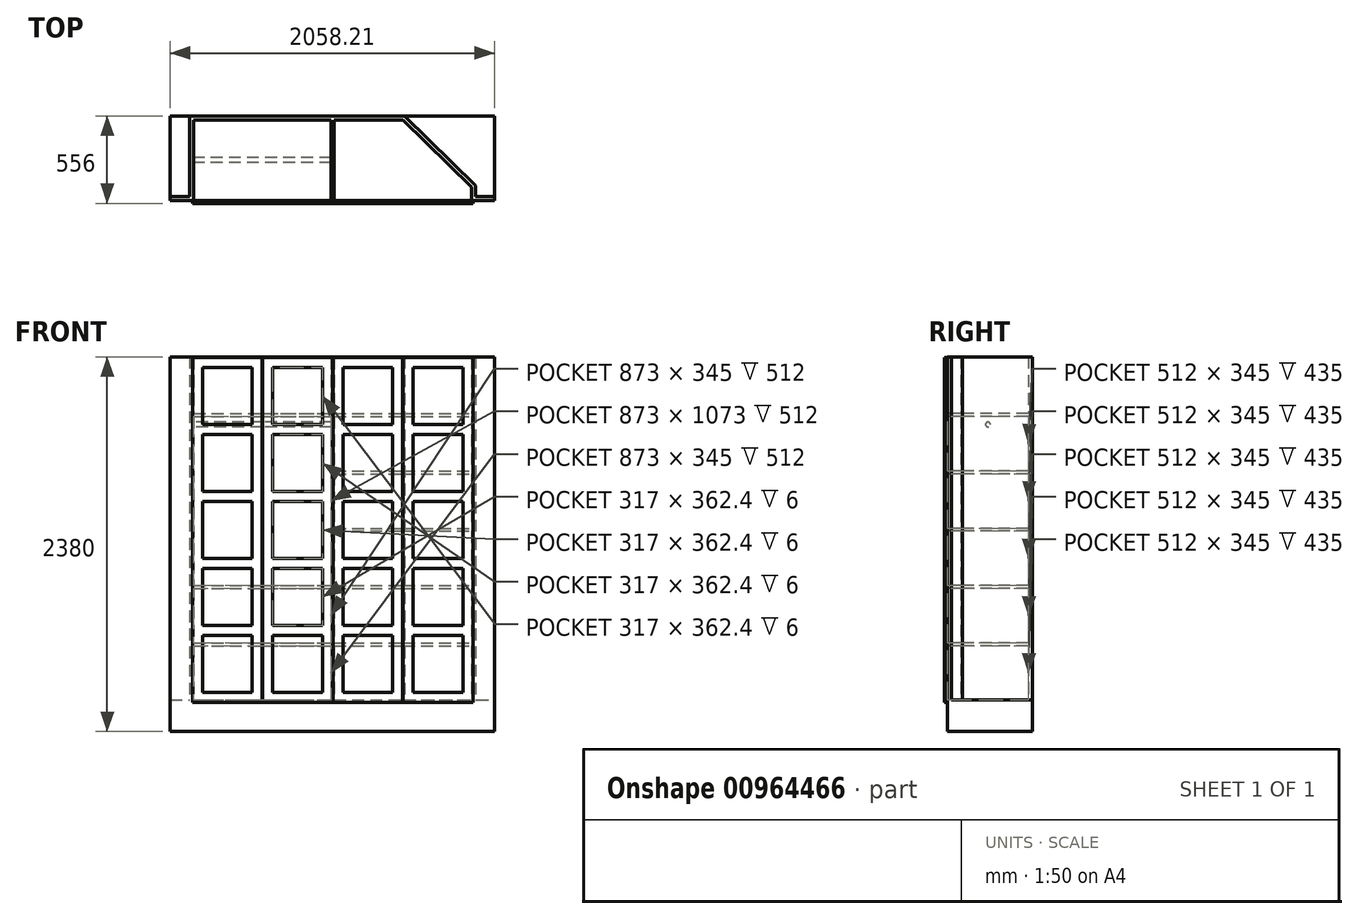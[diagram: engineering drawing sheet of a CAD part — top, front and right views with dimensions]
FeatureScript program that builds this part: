
annotation { "Feature Type Name" : "Feature", "Feature Type Description" : "" }
export const myFeature = defineFeature(function(context is Context, id is Id, definition is map)
    precondition{}
    {
        {
            var Q0;
            Q0=qCreatedBy(makeId("Top.planeOp"),FACE);
            var sketch = newSketch(context, id + "F0", { "sketchPlane" : qUnion([Q0])});
            skLineSegment(sketch, "E0", {"start": v(-882.5, 0) * mm, "end": v(882.5, 0) * mm, "construction": true});
            skLineSegment(sketch, "E1", {"start": v(-882.5, 0) * mm, "end": v(-1031.49, 0) * mm});
            skLineSegment(sketch, "E2", {"start": v(-882.5, 0) * mm, "end": v(-882.5, 512) * mm});
            skLineSegment(sketch, "E3", {"start": v(-882.5, 512) * mm, "end": v(445.5, 512) * mm});
            skLineSegment(sketch, "E4", {"start": v(445.5, 512) * mm, "end": v(882.5, 85) * mm});
            skLineSegment(sketch, "E5", {"start": v(882.5, 0) * mm, "end": v(882.5, 85) * mm});
            skLineSegment(sketch, "E6", {"start": v(882.5, 0) * mm, "end": v(1026.72, 0) * mm});
            skLineSegment(sketch, "E7.0", {"start": v(-907.5, 25) * mm, "end": v(-1031.49, 25) * mm});
            skLineSegment(sketch, "E7.1", {"start": v(-907.5, 25) * mm, "end": v(-907.5, 537) * mm});
            skLineSegment(sketch, "E7.2", {"start": v(907.5, 25) * mm, "end": v(1026.72, 25) * mm});
            skLineSegment(sketch, "E7.3", {"start": v(907.5, 25) * mm, "end": v(907.5, 95.53) * mm});
            skLineSegment(sketch, "E7.4", {"start": v(455.69, 537) * mm, "end": v(907.5, 95.53) * mm});
            skLineSegment(sketch, "E7.5", {"start": v(-907.5, 537) * mm, "end": v(455.69, 537) * mm});
            skLineSegment(sketch, "E8", {"start": v(-1031.49, 0) * mm, "end": v(-1031.49, 25) * mm});
            skLineSegment(sketch, "E9", {"start": v(1026.72, 0) * mm, "end": v(1026.72, 25) * mm});
            skSolve(sketch);
        }
        {
            var Q0;
            Q0 = qSketchRegion(id + "F0", true);
            extrude(context, id + "F1", {"entities" : qUnion([Q0]), "depth" : 2180 * mm, "offsetDistance" : 25 * mm});
        }
        {
            var Q0;
            Q0=makeQuery(id+"F1.opExtrude","CAP_FACE",FACE,{"disambiguationData":[OSD([sQuery(id+"F0.wireOp",EDGE,"E1"),sQuery(id+"F0.wireOp",EDGE,"E2"),sQuery(id+"F0.wireOp",EDGE,"E3"),sQuery(id+"F0.wireOp",EDGE,"E4"),sQuery(id+"F0.wireOp",EDGE,"E5"),sQuery(id+"F0.wireOp",EDGE,"E6"),sQuery(id+"F0.wireOp",EDGE,"E7.0"),sQuery(id+"F0.wireOp",EDGE,"E7.1"),sQuery(id+"F0.wireOp",EDGE,"E7.2"),sQuery(id+"F0.wireOp",EDGE,"E7.3"),sQuery(id+"F0.wireOp",EDGE,"E7.4"),sQuery(id+"F0.wireOp",EDGE,"E7.5"),sQuery(id+"F0.wireOp",EDGE,"E8"),sQuery(id+"F0.wireOp",EDGE,"E9")])],"isStart":true});
            var sketch = newSketch(context, id + "F2", { "sketchPlane" : qUnion([Q0])});
            skLineSegment(sketch, "E10.bottom", {"start": v(-1031.49, 0) * mm, "end": v(1026.72, 0) * mm});
            skLineSegment(sketch, "E10.top", {"start": v(-1031.49, -537) * mm, "end": v(1026.72, -537) * mm});
            skLineSegment(sketch, "E10.left", {"start": v(-1031.49, 0) * mm, "end": v(-1031.49, -537) * mm});
            skLineSegment(sketch, "E10.right", {"start": v(1026.72, 0) * mm, "end": v(1026.72, -537) * mm});
            skSolve(sketch);
        }
        {
            var Q0;
            Q0 = qSketchRegion(id + "F2", true);
            extrude(context, id + "F3", {"entities" : qUnion([Q0]), "operationType" : NewBodyOperationType.ADD, "depth" : 200 * mm, "offsetDistance" : 25 * mm});
        }
        {
            var Q0;
            {var subQ0=sQuery(id+"F2.wireOp",EDGE,"E10.bottom");Q0=makeQuery(id+"F3.boolean.opBoolean","SPLIT",FACE,{"disambiguationData":[TD([makeQuery(id+"F1.opExtrude","SWEPT_FACE",FACE,{"disambiguationData":[OSD([sQuery(id+"F0.wireOp",EDGE,"E1")])]})])],"derivedFrom":makeQuery(id+"F3.opExtrude","CAP_FACE",FACE,{"disambiguationData":[OSD([subQ0,sQuery(id+"F2.wireOp",EDGE,"E10.top"),sQuery(id+"F2.wireOp",EDGE,"E10.left"),sQuery(id+"F2.wireOp",EDGE,"E10.right")])],"isStart":true})});}
            var sketch = newSketch(context, id + "F4", { "sketchPlane" : qUnion([Q0])});
            skLineSegment(sketch, "E11.bottom", {"start": v(-9.5, 0) * mm, "end": v(9.5, 0) * mm});
            skLineSegment(sketch, "E11.top", {"start": v(-9.5, 512) * mm, "end": v(9.5, 512) * mm});
            skLineSegment(sketch, "E11.left", {"start": v(-9.5, 0) * mm, "end": v(-9.5, 512) * mm});
            skLineSegment(sketch, "E11.right", {"start": v(9.5, 0) * mm, "end": v(9.5, 512) * mm});
            skSolve(sketch);
        }
        {
            var Q0;
            Q0 = qSketchRegion(id + "F4", true);
            var Q1;
            Q1=makeQuery(id+"F1.opExtrude","CAP_FACE",FACE,{"disambiguationData":[OSD([sQuery(id+"F0.wireOp",EDGE,"E1"),sQuery(id+"F0.wireOp",EDGE,"E2"),sQuery(id+"F0.wireOp",EDGE,"E3"),sQuery(id+"F0.wireOp",EDGE,"E4"),sQuery(id+"F0.wireOp",EDGE,"E5"),sQuery(id+"F0.wireOp",EDGE,"E6"),sQuery(id+"F0.wireOp",EDGE,"E7.0"),sQuery(id+"F0.wireOp",EDGE,"E7.1"),sQuery(id+"F0.wireOp",EDGE,"E7.2"),sQuery(id+"F0.wireOp",EDGE,"E7.3"),sQuery(id+"F0.wireOp",EDGE,"E7.4"),sQuery(id+"F0.wireOp",EDGE,"E7.5"),sQuery(id+"F0.wireOp",EDGE,"E8"),sQuery(id+"F0.wireOp",EDGE,"E9")])],"isStart":false});
            extrude(context, id + "F5", {"entities" : qUnion([Q0]), "operationType" : NewBodyOperationType.ADD, "endBound" : BoundingType.UP_TO_SURFACE, "depth" : 25 * mm, "endBoundEntityFace" : qUnion([Q1]), "offsetDistance" : 25 * mm});
        }
        {
            var Q0;
            Q0=makeQuery(id+"F5.boolean.opBoolean","MERGE",FACE,{"derivedFrom":[makeQuery(id+"F3.boolean.opBoolean","MERGE",FACE,{"derivedFrom":[makeQuery(id+"F1.opExtrude","SWEPT_FACE",FACE,{"disambiguationData":[OSD([sQuery(id+"F0.wireOp",EDGE,"E1")])]}),makeQuery(id+"F1.opExtrude","SWEPT_FACE",FACE,{"disambiguationData":[OSD([sQuery(id+"F0.wireOp",EDGE,"E6")])]}),makeQuery(id+"F3.opExtrude","SWEPT_FACE",FACE,{"disambiguationData":[OSD([sQuery(id+"F2.wireOp",EDGE,"E10.bottom")])]})]}),makeQuery(id+"F5.opExtrude","SWEPT_FACE",FACE,{"disambiguationData":[OSD([sQuery(id+"F4.wireOp",EDGE,"E11.bottom")])]}),makeQuery(id+"F5.opExtrude","SWEPT_FACE",FACE,{"disambiguationData":[OSD([sQuery(id+"F4.wireOp",EDGE,"kJ6FKThs-MoNL-kqar-oXPB-ncLJq9slYm2o.bottom")])]}),makeQuery(id+"F5.opExtrude","SWEPT_FACE",FACE,{"disambiguationData":[OSD([sQuery(id+"F4.wireOp",EDGE,"Q5dsoZYq-HTbt-CrDa-Fhxc-pEQLqIX1TYuc.bottom")])]})]});
            var sketch = newSketch(context, id + "F6", { "sketchPlane" : qUnion([Q0])});
            skLineSegment(sketch, "E12.bottom", {"start": v(-444.5, -15) * mm, "end": v(-1.5, -15) * mm});
            skLineSegment(sketch, "E12.top", {"start": v(-444.5, 2175) * mm, "end": v(-1.5, 2175) * mm});
            skLineSegment(sketch, "E12.left", {"start": v(-444.5, -15) * mm, "end": v(-444.5, 2175) * mm});
            skLineSegment(sketch, "E12.right", {"start": v(-1.5, -15) * mm, "end": v(-1.5, 2175) * mm});
            skLineSegment(sketch, "E13.bottom", {"start": v(-1.5, -15) * mm, "end": v(-444.5, -15) * mm});
            skLineSegment(sketch, "E13.top", {"start": v(-1.5, 2175) * mm, "end": v(-444.5, 2175) * mm});
            skLineSegment(sketch, "E13.right", {"start": v(-890.5, -15) * mm, "end": v(-890.5, 2175) * mm});
            skLineSegment(sketch, "E14.left", {"start": v(1.5, -15) * mm, "end": v(1.5, 2175) * mm});
            skLineSegment(sketch, "E14.right", {"start": v(-1.5, -15) * mm, "end": v(-1.5, 2195) * mm});
            skLineSegment(sketch, "E15.bottom", {"start": v(447.5, -15) * mm, "end": v(890.5, -15) * mm});
            skLineSegment(sketch, "E15.top", {"start": v(447.5, 2175) * mm, "end": v(890.5, 2175) * mm});
            skLineSegment(sketch, "E15.left", {"start": v(447.5, -15) * mm, "end": v(447.5, 2175) * mm});
            skLineSegment(sketch, "E15.right", {"start": v(890.5, -15) * mm, "end": v(890.5, 2175) * mm});
            skLineSegment(sketch, "E16", {"start": v(-447.5, -15) * mm, "end": v(-447.5, 2175) * mm});
            skLineSegment(sketch, "E17.trimOffspring", {"start": v(-447.5, 2175) * mm, "end": v(-890.5, 2175) * mm});
            skLineSegment(sketch, "E18.trimOffspring", {"start": v(-447.5, -15) * mm, "end": v(-890.5, -15) * mm});
            skLineSegment(sketch, "E19", {"start": v(1.5, -15) * mm, "end": v(444.5, -15) * mm});
            skLineSegment(sketch, "E20", {"start": v(444.5, -15) * mm, "end": v(444.5, 2175) * mm});
            skLineSegment(sketch, "E21", {"start": v(1.5, 2175) * mm, "end": v(444.5, 2175) * mm});
            skSolve(sketch);
        }
        {
            var Q0;
            Q0 = qSketchRegion(id + "F6", true);
            extrude(context, id + "F7", {"entities" : qUnion([Q0]), "operationType" : NewBodyOperationType.ADD, "depth" : 19 * mm, "offsetDistance" : 25 * mm});
        }
        {
            var Q0;
            Q0=makeQuery(id+"F7.opExtrude","CAP_FACE",FACE,{"disambiguationData":[OSD([sQuery(id+"F6.wireOp",EDGE,"E13.bottom"),sQuery(id+"F6.wireOp",EDGE,"E13.top"),sQuery(id+"F6.wireOp",EDGE,"E12.right"),sQuery(id+"F6.wireOp",EDGE,"E13.right")])],"isStart":false});
            var sketch = newSketch(context, id + "F8", { "sketchPlane" : qUnion([Q0])});
            skLineSegment(sketch, "E22.bottom", {"start": v(-827.5, 2112) * mm, "end": v(-510.5, 2112) * mm});
            skLineSegment(sketch, "E22.top", {"start": v(-827.5, 1749.6) * mm, "end": v(-510.5, 1749.6) * mm});
            skLineSegment(sketch, "E22.left", {"start": v(-827.5, 2112) * mm, "end": v(-827.5, 1749.6) * mm});
            skLineSegment(sketch, "E22.right", {"start": v(-510.5, 2112) * mm, "end": v(-510.5, 1749.6) * mm});
            skLineSegment(sketch, "E23.bottom", {"start": v(-827.5, 1686.6) * mm, "end": v(-510.5, 1686.6) * mm});
            skLineSegment(sketch, "E23.top", {"start": v(-827.5, 1324.2) * mm, "end": v(-510.5, 1324.2) * mm});
            skLineSegment(sketch, "E23.left", {"start": v(-827.5, 1686.6) * mm, "end": v(-827.5, 1324.2) * mm});
            skLineSegment(sketch, "E23.right", {"start": v(-510.5, 1686.6) * mm, "end": v(-510.5, 1324.2) * mm});
            skLineSegment(sketch, "E24.bottom", {"start": v(-827.5, 1261.2) * mm, "end": v(-510.5, 1261.2) * mm});
            skLineSegment(sketch, "E24.top", {"start": v(-827.5, 898.8) * mm, "end": v(-510.5, 898.8) * mm});
            skLineSegment(sketch, "E24.left", {"start": v(-827.5, 1261.2) * mm, "end": v(-827.5, 898.8) * mm});
            skLineSegment(sketch, "E24.right", {"start": v(-510.5, 1261.2) * mm, "end": v(-510.5, 898.8) * mm});
            skLineSegment(sketch, "E25.bottom", {"start": v(-827.5, 835.8) * mm, "end": v(-510.5, 835.8) * mm});
            skLineSegment(sketch, "E25.top", {"start": v(-827.5, 473.4) * mm, "end": v(-510.5, 473.4) * mm});
            skLineSegment(sketch, "E25.left", {"start": v(-827.5, 835.8) * mm, "end": v(-827.5, 473.4) * mm});
            skLineSegment(sketch, "E25.right", {"start": v(-510.5, 835.8) * mm, "end": v(-510.5, 473.4) * mm});
            skLineSegment(sketch, "E26.bottom", {"start": v(-827.5, 410.4) * mm, "end": v(-510.5, 410.4) * mm});
            skLineSegment(sketch, "E26.top", {"start": v(-827.5, 48) * mm, "end": v(-510.5, 48) * mm});
            skLineSegment(sketch, "E26.left", {"start": v(-827.5, 410.4) * mm, "end": v(-827.5, 48) * mm});
            skLineSegment(sketch, "E26.right", {"start": v(-510.5, 410.4) * mm, "end": v(-510.5, 48) * mm});
            skLineSegment(sketch, "E27.bottom", {"start": v(-381.5, 2112) * mm, "end": v(-64.5, 2112) * mm});
            skLineSegment(sketch, "E27.top", {"start": v(-381.5, 1749.6) * mm, "end": v(-64.5, 1749.6) * mm});
            skLineSegment(sketch, "E27.left", {"start": v(-381.5, 2112) * mm, "end": v(-381.5, 1749.6) * mm});
            skLineSegment(sketch, "E28.left", {"start": v(64.5, 2112) * mm, "end": v(64.5, 1749.6) * mm});
            skLineSegment(sketch, "E28.right", {"start": v(-64.5, 2112) * mm, "end": v(-64.5, 1749.6) * mm});
            skLineSegment(sketch, "E29.bottom", {"start": v(510.5, 2112) * mm, "end": v(827.5, 2112) * mm});
            skLineSegment(sketch, "E29.top", {"start": v(510.5, 1749.6) * mm, "end": v(827.5, 1749.6) * mm});
            skLineSegment(sketch, "E29.left", {"start": v(510.5, 2112) * mm, "end": v(510.5, 1749.6) * mm});
            skLineSegment(sketch, "E29.right", {"start": v(827.5, 2112) * mm, "end": v(827.5, 1749.6) * mm});
            skLineSegment(sketch, "E30.bottom", {"start": v(-381.5, 1686.6) * mm, "end": v(-64.5, 1686.6) * mm});
            skLineSegment(sketch, "E30.top", {"start": v(-381.5, 1324.2) * mm, "end": v(-64.5, 1324.2) * mm});
            skLineSegment(sketch, "E30.left", {"start": v(-381.5, 1686.6) * mm, "end": v(-381.5, 1324.2) * mm});
            skLineSegment(sketch, "E31.left", {"start": v(64.5, 1686.6) * mm, "end": v(64.5, 1324.2) * mm});
            skLineSegment(sketch, "E31.right", {"start": v(-64.5, 1686.6) * mm, "end": v(-64.5, 1324.2) * mm});
            skLineSegment(sketch, "E32.bottom", {"start": v(510.5, 1686.6) * mm, "end": v(827.5, 1686.6) * mm});
            skLineSegment(sketch, "E32.top", {"start": v(510.5, 1324.2) * mm, "end": v(827.5, 1324.2) * mm});
            skLineSegment(sketch, "E32.left", {"start": v(510.5, 1686.6) * mm, "end": v(510.5, 1324.2) * mm});
            skLineSegment(sketch, "E32.right", {"start": v(827.5, 1686.6) * mm, "end": v(827.5, 1324.2) * mm});
            skLineSegment(sketch, "E33.bottom", {"start": v(-381.5, 1261.2) * mm, "end": v(-64.5, 1261.2) * mm});
            skLineSegment(sketch, "E33.top", {"start": v(-381.5, 898.8) * mm, "end": v(-64.5, 898.8) * mm});
            skLineSegment(sketch, "E33.left", {"start": v(-381.5, 1261.2) * mm, "end": v(-381.5, 898.8) * mm});
            skLineSegment(sketch, "E34.left", {"start": v(64.5, 1261.2) * mm, "end": v(64.5, 898.8) * mm});
            skLineSegment(sketch, "E34.right", {"start": v(-64.5, 1261.2) * mm, "end": v(-64.5, 898.8) * mm});
            skLineSegment(sketch, "E35.bottom", {"start": v(510.5, 1261.2) * mm, "end": v(827.5, 1261.2) * mm});
            skLineSegment(sketch, "E35.top", {"start": v(510.5, 898.8) * mm, "end": v(827.5, 898.8) * mm});
            skLineSegment(sketch, "E35.left", {"start": v(510.5, 1261.2) * mm, "end": v(510.5, 898.8) * mm});
            skLineSegment(sketch, "E35.right", {"start": v(827.5, 1261.2) * mm, "end": v(827.5, 898.8) * mm});
            skLineSegment(sketch, "E36.bottom", {"start": v(-381.5, 835.8) * mm, "end": v(-64.5, 835.8) * mm});
            skLineSegment(sketch, "E36.top", {"start": v(-381.5, 473.4) * mm, "end": v(-64.5, 473.4) * mm});
            skLineSegment(sketch, "E36.left", {"start": v(-381.5, 835.8) * mm, "end": v(-381.5, 473.4) * mm});
            skLineSegment(sketch, "E37.left", {"start": v(64.5, 835.8) * mm, "end": v(64.5, 473.4) * mm});
            skLineSegment(sketch, "E37.right", {"start": v(-64.5, 835.8) * mm, "end": v(-64.5, 473.4) * mm});
            skLineSegment(sketch, "E38.bottom", {"start": v(510.5, 835.8) * mm, "end": v(827.5, 835.8) * mm});
            skLineSegment(sketch, "E38.top", {"start": v(510.5, 473.4) * mm, "end": v(827.5, 473.4) * mm});
            skLineSegment(sketch, "E38.left", {"start": v(510.5, 835.8) * mm, "end": v(510.5, 473.4) * mm});
            skLineSegment(sketch, "E38.right", {"start": v(827.5, 835.8) * mm, "end": v(827.5, 473.4) * mm});
            skLineSegment(sketch, "E39.bottom", {"start": v(-381.5, 410.4) * mm, "end": v(-64.5, 410.4) * mm});
            skLineSegment(sketch, "E39.top", {"start": v(-381.5, 48) * mm, "end": v(-64.5, 48) * mm});
            skLineSegment(sketch, "E39.left", {"start": v(-381.5, 410.4) * mm, "end": v(-381.5, 48) * mm});
            skLineSegment(sketch, "E40.left", {"start": v(64.5, 410.4) * mm, "end": v(64.5, 48) * mm});
            skLineSegment(sketch, "E40.right", {"start": v(-64.5, 410.4) * mm, "end": v(-64.5, 48) * mm});
            skLineSegment(sketch, "E41.bottom", {"start": v(510.5, 410.4) * mm, "end": v(827.5, 410.4) * mm});
            skLineSegment(sketch, "E41.top", {"start": v(510.5, 48) * mm, "end": v(827.5, 48) * mm});
            skLineSegment(sketch, "E41.left", {"start": v(510.5, 410.4) * mm, "end": v(510.5, 48) * mm});
            skLineSegment(sketch, "E41.right", {"start": v(827.5, 410.4) * mm, "end": v(827.5, 48) * mm});
            skLineSegment(sketch, "E42", {"start": v(64.5, 2112) * mm, "end": v(381.5, 2112) * mm});
            skLineSegment(sketch, "E43", {"start": v(381.5, 2112) * mm, "end": v(381.5, 1749.6) * mm});
            skLineSegment(sketch, "E44", {"start": v(64.5, 48) * mm, "end": v(381.5, 48) * mm});
            skLineSegment(sketch, "E45", {"start": v(64.5, 410.4) * mm, "end": v(381.5, 410.4) * mm});
            skLineSegment(sketch, "E46", {"start": v(64.5, 473.4) * mm, "end": v(381.5, 473.4) * mm});
            skLineSegment(sketch, "E47.trimOffspring", {"start": v(381.5, 410.4) * mm, "end": v(381.5, 48) * mm});
            skLineSegment(sketch, "E48", {"start": v(64.5, 835.8) * mm, "end": v(381.5, 835.8) * mm});
            skLineSegment(sketch, "E49", {"start": v(64.5, 898.8) * mm, "end": v(381.5, 898.8) * mm});
            skLineSegment(sketch, "E50.trimOffspring", {"start": v(381.5, 835.8) * mm, "end": v(381.5, 473.4) * mm});
            skLineSegment(sketch, "E51", {"start": v(64.5, 1261.2) * mm, "end": v(381.5, 1261.2) * mm});
            skLineSegment(sketch, "E52", {"start": v(64.5, 1324.2) * mm, "end": v(381.5, 1324.2) * mm});
            skLineSegment(sketch, "E53.trimOffspring", {"start": v(381.5, 1261.2) * mm, "end": v(381.5, 898.8) * mm});
            skLineSegment(sketch, "E54", {"start": v(64.5, 1686.6) * mm, "end": v(381.5, 1686.6) * mm});
            skLineSegment(sketch, "E55", {"start": v(64.5, 1749.6) * mm, "end": v(381.5, 1749.6) * mm});
            skLineSegment(sketch, "E56.trimOffspring", {"start": v(381.5, 1686.6) * mm, "end": v(381.5, 1324.2) * mm});
            skSolve(sketch);
        }
        {
            var Q0;
            Q0 = qSketchRegion(id + "F8", true);
            extrude(context, id + "F9", {"entities" : qUnion([Q0]), "operationType" : NewBodyOperationType.REMOVE, "oppositeDirection" : true, "depth" : 6 * mm, "offsetDistance" : 25 * mm});
        }
        {
            var Q0;
            Q0=makeQuery(id+"F5.boolean.opBoolean","MERGE",FACE,{"derivedFrom":[makeQuery(id+"F3.boolean.opBoolean","MERGE",FACE,{"derivedFrom":[makeQuery(id+"F1.opExtrude","SWEPT_FACE",FACE,{"disambiguationData":[OSD([sQuery(id+"F0.wireOp",EDGE,"E1")])]}),makeQuery(id+"F1.opExtrude","SWEPT_FACE",FACE,{"disambiguationData":[OSD([sQuery(id+"F0.wireOp",EDGE,"E6")])]}),makeQuery(id+"F3.opExtrude","SWEPT_FACE",FACE,{"disambiguationData":[OSD([sQuery(id+"F2.wireOp",EDGE,"E10.bottom")])]})]}),makeQuery(id+"F5.opExtrude","SWEPT_FACE",FACE,{"disambiguationData":[OSD([sQuery(id+"F4.wireOp",EDGE,"E11.bottom")])]})]});
            var sketch = newSketch(context, id + "F10", { "sketchPlane" : qUnion([Q0])});
            skLineSegment(sketch, "E57.bottom", {"start": v(-882.5, 345) * mm, "end": v(-9.5, 345) * mm});
            skLineSegment(sketch, "E57.top", {"start": v(-882.5, 364) * mm, "end": v(-9.5, 364) * mm});
            skLineSegment(sketch, "E57.left", {"start": v(-882.5, 345) * mm, "end": v(-882.5, 364) * mm});
            skLineSegment(sketch, "E57.right", {"start": v(-9.5, 345) * mm, "end": v(-9.5, 364) * mm});
            skLineSegment(sketch, "E58.bottom", {"start": v(-882.5, 1820) * mm, "end": v(-9.5, 1820) * mm});
            skLineSegment(sketch, "E58.top", {"start": v(-882.5, 1801) * mm, "end": v(-9.5, 1801) * mm});
            skLineSegment(sketch, "E58.left", {"start": v(-882.5, 1820) * mm, "end": v(-882.5, 1801) * mm});
            skLineSegment(sketch, "E58.right", {"start": v(-9.5, 1820) * mm, "end": v(-9.5, 1801) * mm});
            skLineSegment(sketch, "E59.bottom", {"start": v(-882.5, 709) * mm, "end": v(-9.5, 709) * mm});
            skLineSegment(sketch, "E59.top", {"start": v(-882.5, 728) * mm, "end": v(-9.5, 728) * mm});
            skLineSegment(sketch, "E59.left", {"start": v(-882.5, 709) * mm, "end": v(-882.5, 728) * mm});
            skLineSegment(sketch, "E59.right", {"start": v(-9.5, 709) * mm, "end": v(-9.5, 728) * mm});
            skLineSegment(sketch, "E60.bottom", {"start": v(9.5, 364) * mm, "end": v(882.5, 364) * mm});
            skLineSegment(sketch, "E60.top", {"start": v(9.5, 345) * mm, "end": v(882.5, 345) * mm});
            skLineSegment(sketch, "E60.left", {"start": v(9.5, 364) * mm, "end": v(9.5, 345) * mm});
            skLineSegment(sketch, "E60.right", {"start": v(882.5, 364) * mm, "end": v(882.5, 345) * mm});
            skLineSegment(sketch, "E61.bottom", {"start": v(9.5, 728) * mm, "end": v(882.5, 728) * mm});
            skLineSegment(sketch, "E61.top", {"start": v(9.5, 709) * mm, "end": v(882.5, 709) * mm});
            skLineSegment(sketch, "E61.left", {"start": v(9.5, 728) * mm, "end": v(9.5, 709) * mm});
            skLineSegment(sketch, "E61.right", {"start": v(882.5, 728) * mm, "end": v(882.5, 709) * mm});
            skLineSegment(sketch, "E62.bottom", {"start": v(9.5, 1092) * mm, "end": v(882.5, 1092) * mm});
            skLineSegment(sketch, "E62.top", {"start": v(9.5, 1073) * mm, "end": v(882.5, 1073) * mm});
            skLineSegment(sketch, "E62.left", {"start": v(9.5, 1092) * mm, "end": v(9.5, 1073) * mm});
            skLineSegment(sketch, "E62.right", {"start": v(882.5, 1092) * mm, "end": v(882.5, 1073) * mm});
            skLineSegment(sketch, "E63.bottom", {"start": v(9.5, 1456) * mm, "end": v(882.5, 1456) * mm});
            skLineSegment(sketch, "E63.top", {"start": v(9.5, 1437) * mm, "end": v(882.5, 1437) * mm});
            skLineSegment(sketch, "E63.left", {"start": v(9.5, 1456) * mm, "end": v(9.5, 1437) * mm});
            skLineSegment(sketch, "E63.right", {"start": v(882.5, 1456) * mm, "end": v(882.5, 1437) * mm});
            skLineSegment(sketch, "E64.bottom", {"start": v(9.5, 1820) * mm, "end": v(882.5, 1820) * mm});
            skLineSegment(sketch, "E64.top", {"start": v(9.5, 1801) * mm, "end": v(882.5, 1801) * mm});
            skLineSegment(sketch, "E64.left", {"start": v(9.5, 1820) * mm, "end": v(9.5, 1801) * mm});
            skLineSegment(sketch, "E64.right", {"start": v(882.5, 1820) * mm, "end": v(882.5, 1801) * mm});
            skSolve(sketch);
        }
        {
            var Q0;
            Q0 = qSketchRegion(id + "F10", true);
            extrude(context, id + "F11", {"entities" : qUnion([Q0]), "operationType" : NewBodyOperationType.ADD, "endBound" : BoundingType.UP_TO_NEXT, "oppositeDirection" : true, "depth" : 25 * mm, "offsetDistance" : 25 * mm});
        }
        {
            var Q0;
            {var subQ0=sQuery(id+"F10.wireOp",EDGE,"E58.top");Q0=makeQuery(id+"F11.boolean.opBoolean","SPLIT",FACE,{"disambiguationData":[TD([makeQuery(id+"F11.opExtrude","SWEPT_FACE",FACE,{"disambiguationData":[OSD([subQ0])]})])],"derivedFrom":makeQuery(id+"F1.opExtrude","SWEPT_FACE",FACE,{"disambiguationData":[OSD([sQuery(id+"F0.wireOp",EDGE,"E2")])]})});}
            var sketch = newSketch(context, id + "F12", { "sketchPlane" : qUnion([Q0])});
            skCircle(sketch, "E65", {"center": v(256, 1751) * mm, "radius": 15 * mm});
            skSolve(sketch);
        }
        {
            var Q0;
            Q0 = qSketchRegion(id + "F12", true);
            extrude(context, id + "F13", {"entities" : qUnion([Q0]), "operationType" : NewBodyOperationType.ADD, "endBound" : BoundingType.UP_TO_NEXT, "depth" : 25 * mm, "offsetDistance" : 25 * mm});
        }
    });
